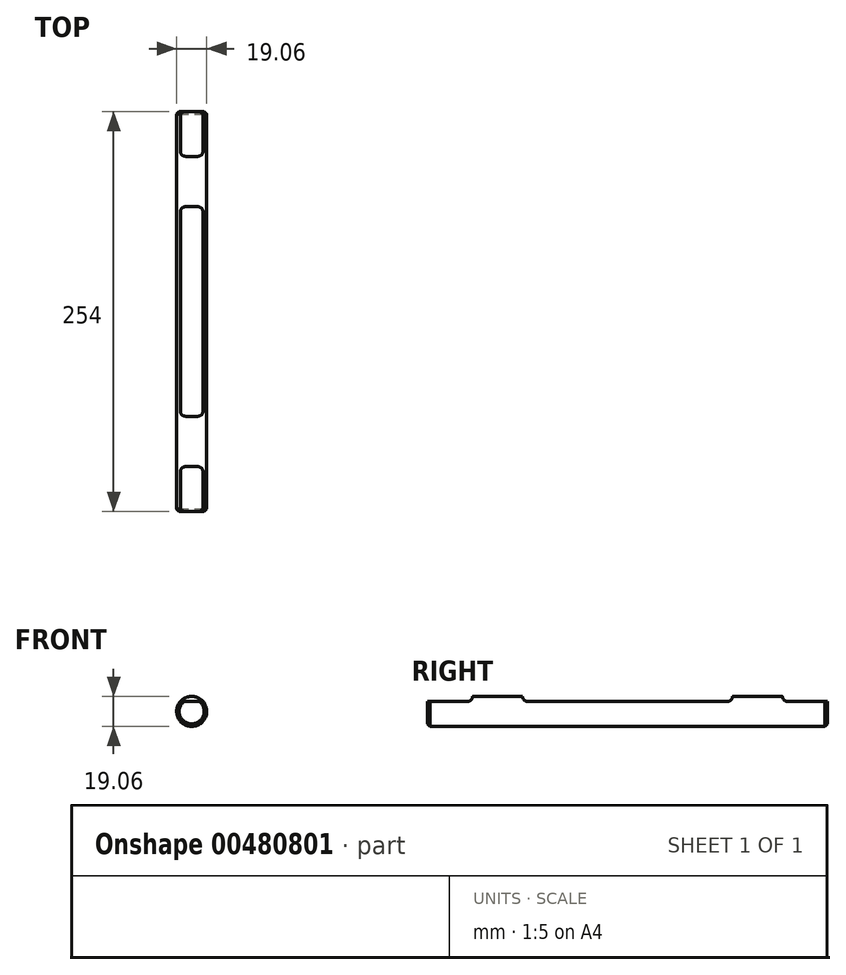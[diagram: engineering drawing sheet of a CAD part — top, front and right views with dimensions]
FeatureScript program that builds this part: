
annotation { "Feature Type Name" : "Feature", "Feature Type Description" : "" }
export const myFeature = defineFeature(function(context is Context, id is Id, definition is map)
    precondition{}
    {
        {
            var Q0;
            Q0=qCreatedBy(makeId("Front.planeOp"),FACE);
            var sketch = newSketch(context, id + "F0", { "sketchPlane" : qUnion([Q0])});
            skCircle(sketch, "E0", {"center": v(0, 0) * mm, "radius": 9.53 * mm});
            skSolve(sketch);
        }
        {
            var Q0;
            Q0=makeQuery(id+"F0.imprint","IMPRINT",FACE,{"disambiguationData":[TD([[makeQuery(id+"F0.imprint","IMPRINT",EDGE,{"derivedFrom":sQuery(id+"F0.wireOp",EDGE,"E0")}),1.0]])]});
            extrude(context, id + "F1", {"entities" : qUnion([Q0]), "endBound" : BoundingType.SYMMETRIC, "depth" : 254 * mm});
        }
        {
            var Q0;
            Q0=qCreatedBy(makeId("Right.planeOp"),FACE);
            var sketch = newSketch(context, id + "F2", { "sketchPlane" : qUnion([Q0])});
            skLineSegment(sketch, "E1.bottom", {"start": v(-127, 9.53) * mm, "end": v(-98.42, 9.53) * mm});
            skLineSegment(sketch, "E1.top", {"start": v(-127, 6.35) * mm, "end": v(-98.42, 6.35) * mm});
            skLineSegment(sketch, "E1.left", {"start": v(-127, 9.53) * mm, "end": v(-127, 6.35) * mm});
            skLineSegment(sketch, "E1.right", {"start": v(-98.42, 9.52) * mm, "end": v(-98.42, 6.35) * mm});
            skLineSegment(sketch, "E2.bottom", {"start": v(-66.67, 6.35) * mm, "end": v(66.68, 6.35) * mm});
            skLineSegment(sketch, "E2.top", {"start": v(-66.67, 9.53) * mm, "end": v(66.68, 9.53) * mm});
            skLineSegment(sketch, "E2.left", {"start": v(-66.67, 6.35) * mm, "end": v(-66.67, 9.53) * mm});
            skLineSegment(sketch, "E2.right", {"start": v(66.68, 6.35) * mm, "end": v(66.68, 9.53) * mm});
            skLineSegment(sketch, "E3.bottom", {"start": v(98.42, 6.35) * mm, "end": v(127, 6.35) * mm});
            skLineSegment(sketch, "E3.top", {"start": v(98.42, 9.53) * mm, "end": v(127, 9.53) * mm});
            skLineSegment(sketch, "E3.left", {"start": v(98.42, 6.35) * mm, "end": v(98.42, 9.53) * mm});
            skLineSegment(sketch, "E3.right", {"start": v(127, 6.35) * mm, "end": v(127, 9.53) * mm});
            skSolve(sketch);
        }
        {
            var Q0;
            Q0=makeQuery(id+"F2.imprint","IMPRINT",FACE,{"disambiguationData":[TD([[makeQuery(id+"F2.imprint","IMPRINT",EDGE,{"derivedFrom":sQuery(id+"F2.wireOp",EDGE,"E2.bottom")}),1.0]])]});
            var Q1;
            Q1=makeQuery(id+"F2.imprint","IMPRINT",FACE,{"disambiguationData":[TD([[makeQuery(id+"F2.imprint","IMPRINT",EDGE,{"derivedFrom":sQuery(id+"F2.wireOp",EDGE,"E1.bottom")}),-1.0]])]});
            var Q2;
            Q2=makeQuery(id+"F2.imprint","IMPRINT",FACE,{"disambiguationData":[TD([[makeQuery(id+"F2.imprint","IMPRINT",EDGE,{"derivedFrom":sQuery(id+"F2.wireOp",EDGE,"E3.bottom")}),1.0]])]});
            extrude(context, id + "F3", {"entities" : qUnion([Q0, Q1, Q2]), "operationType" : NewBodyOperationType.REMOVE, "endBound" : BoundingType.SYMMETRIC, "oppositeDirection" : true, "depth" : 25.4 * mm});
        }
        {
            var Q0;
            Q0=makeQuery(id+"F1.opExtrude","CAP_EDGE",EDGE,{"disambiguationData":[OSD([sQuery(id+"F0.wireOp",EDGE,"E0")])],"isStart":false});
            var Q1;
            Q1=makeQuery(id+"F1.opExtrude","CAP_EDGE",EDGE,{"disambiguationData":[OSD([sQuery(id+"F0.wireOp",EDGE,"E0")])],"isStart":true});
            chamfer(context, id + "F4", {"entities" : qUnion([Q0, Q1]), "width" : 1.52 * mm, "tangentPropagation" : true});
        }
        {
            var Q0;
            Q0=makeQuery(id+"F3.boolean.opBoolean","COPY",EDGE,{"derivedFrom":makeQuery(id+"F3.opExtrude","SWEPT_EDGE",EDGE,{"disambiguationData":[OSD([sQuery(id+"F2.wireOp",EDGE,"E1.top"),sQuery(id+"F2.wireOp",EDGE,"E1.right")])]})});
            var Q1;
            Q1=makeQuery(id+"F3.boolean.opBoolean","COPY",EDGE,{"derivedFrom":makeQuery(id+"F3.opExtrude","SWEPT_EDGE",EDGE,{"disambiguationData":[OSD([sQuery(id+"F2.wireOp",EDGE,"E2.bottom"),sQuery(id+"F2.wireOp",EDGE,"E2.right")])]})});
            var Q2;
            Q2=makeQuery(id+"F3.boolean.opBoolean","COPY",EDGE,{"derivedFrom":makeQuery(id+"F3.opExtrude","SWEPT_EDGE",EDGE,{"disambiguationData":[OSD([sQuery(id+"F2.wireOp",EDGE,"E3.bottom"),sQuery(id+"F2.wireOp",EDGE,"E3.left")])]})});
            var Q3;
            Q3=makeQuery(id+"F3.boolean.opBoolean","COPY",EDGE,{"derivedFrom":makeQuery(id+"F3.opExtrude","SWEPT_EDGE",EDGE,{"disambiguationData":[OSD([sQuery(id+"F2.wireOp",EDGE,"E2.bottom"),sQuery(id+"F2.wireOp",EDGE,"E2.left")])]})});
            fillet(context, id + "F5", {"entities" : qUnion([Q0, Q1, Q2, Q3]), "radius" : 3.17 * mm, "tangentPropagation" : true, "allowEdgeOverflow" : false});
        }
    });
